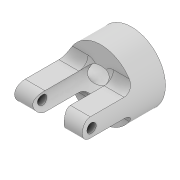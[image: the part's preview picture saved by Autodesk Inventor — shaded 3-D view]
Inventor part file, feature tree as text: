
AUTODESK INVENTOR PART (.ipt)
format: ipt  version: 2020 (Build 240168000, 168)  size: 182,784 bytes
history: native  units: in
note: dims shown in document units (in); Inventor stores cm internally (conversion verified against a paired STEP export)
features: extrude x4, sketch x4, fillet x1, projected_geometry x1
ambient origin geometry x8: Origin, YZ Plane, XZ Plane, XY Plane, X Axis, Y Axis, Z Axis, Center Point
bodies: Solid1 (feature_tree)
feature tree (10):
  extrude  "Extrusion1"  Depth=0.4331in
  extrude  "Extrusion2"  Depth=0.0591in
  fillet  "Fillet1"  Radius=0.1181in
  extrude  "Extrusion3"  Depth=0.3346in TaperAngle=0.0deg
  extrude  "Extrusion4"  Depth=0.0591in
  sketch  "Sketch1"  dims[d0=0.2008in d1=0.4331in]
  sketch  "Sketch2"  dims[d2=0.1969in d3=0.0in d4=0.0591in d5=0.1181in]
  projected_geometry  "Projected Loop1"
  sketch  "Sketch3"  dims[d6=0.0in d7=0.3346in d8=0.0in]
  sketch  "Sketch4"  dims[d9=0.0591in d10=0.0591in d11=0.1654in d12=0.374in d13=0.0in d14=0.374in d15=0.0in]
